# Revit family: ALUMAXI L
name_source: partatom
category: Connessioni strutturali
revit_build: Autodesk Revit 2016 (Build: 20151007_0715(x64)
units: mm (PartAtom-declared; Revit-internal decimal feet)

## family parameters
Attiva taglio nelle viste = No
Condiviso = No
Host = Superficie
Materiale per comportamento modello = Altro
Numero OmniClass = 23.20.40.11.24.14
Taglio con vuoti quando caricato = Sì
Titolo OmniClass = Wood Connectors

## types (10) — shared parameters
Catalogo = Piastre e connettori per legno
Family Version = 1.0.0
Fori ala cemento diametro = 17 mm
Fori ala legno diametro = 7.5 mm  [stored 0.0246063 ft]
Fori anima diametro = 17 mm
Larghezza ala = 130 mm  [stored 0.426509 ft]
Lunghezza anima = 172 mm  [stored 0.564304 ft]
Materiale = <Per categoria>
Produttore = Rotho Blaas srl
Spessore ala = 12 mm  [stored 0.0393701 ft]
Spessore anima = 10 mm  [stored 0.0328084 ft]
URL = http://www.rothoblaas.com
zero-valued in all types: Prospetto di default

## per-type parameters (varying)
| type | Altezza |
| ALUMAXI 384 L | 384 mm  [stored 1.25984 ft] |
| ALUMAXI 512 L | 512 mm  [stored 1.67979 ft] |
| ALUMAXI 640 L | 640 mm  [stored 2.09974 ft] |
| ALUMAXI 768 L | 768 mm |
| ALUMAXI 448 L (da verga ALUMAXI2176L) | 448 mm |
| ALUMAXI 576 L (da verga ALUMAXI2176L) | 576 mm |
| ALUMAXI 704 L (da verga ALUMAXI2176L) | 704 mm |
| ALUMAXI 832 L (da verga ALUMAXI2176L) | 832 mm |
| ALUMAXI 896 L (da verga ALUMAXI2176L) | 896 mm |
| ALUMAXI 960 L (da verga ALUMAXI2176L) | 960 mm |

note: [stored X ft] marks values corroborated as IEEE doubles in the binary element streams (Revit-internal decimal feet)
